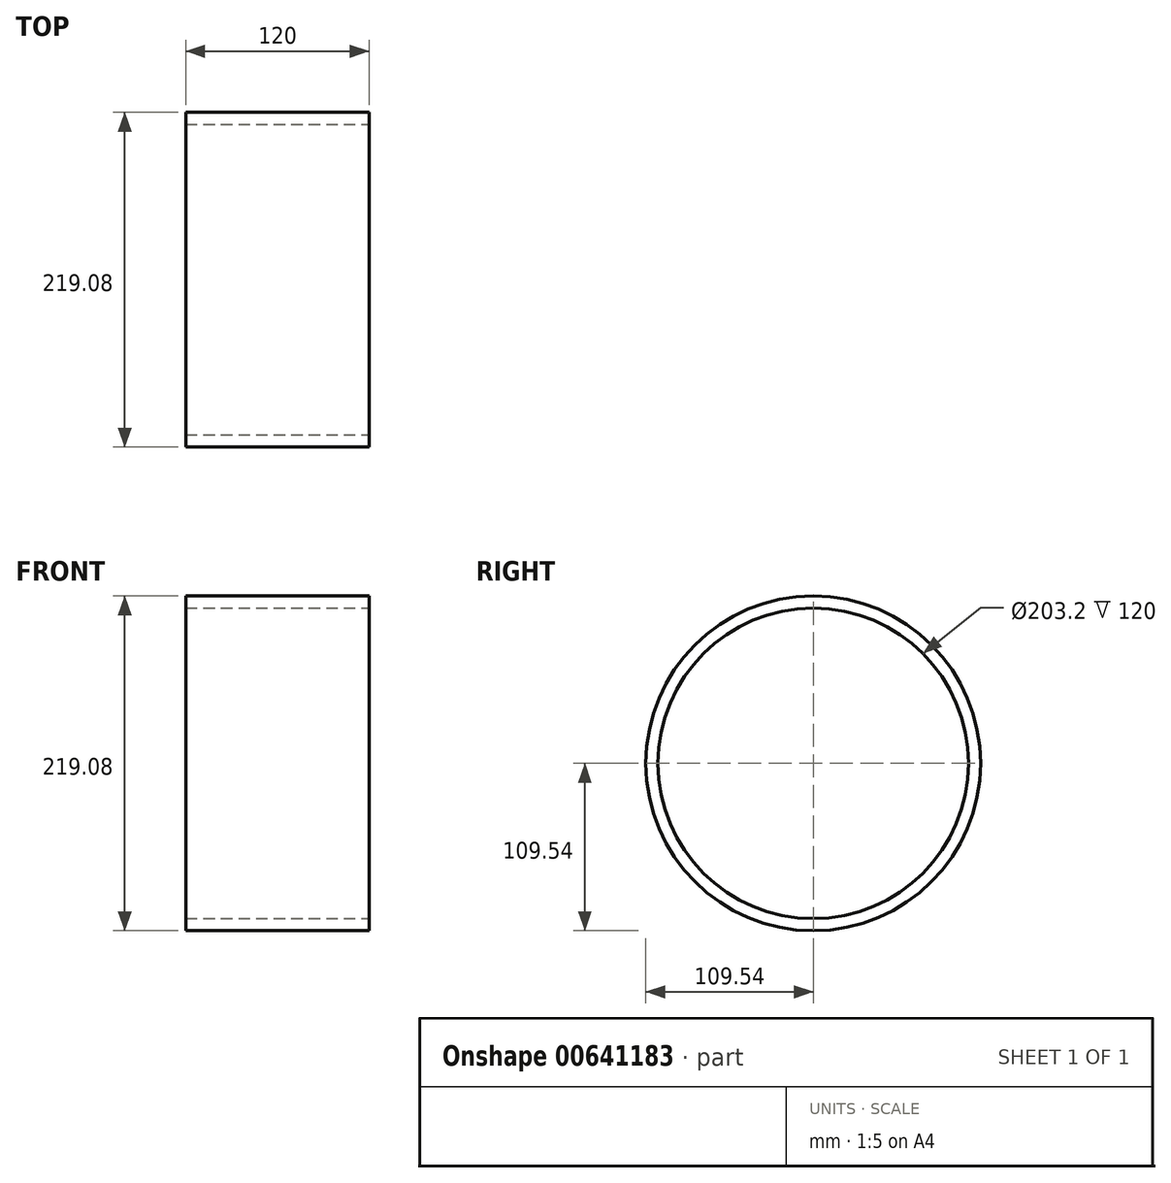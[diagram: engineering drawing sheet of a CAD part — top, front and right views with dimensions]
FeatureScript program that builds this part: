
annotation { "Feature Type Name" : "Feature", "Feature Type Description" : "" }
export const myFeature = defineFeature(function(context is Context, id is Id, definition is map)
    precondition{}
    {
        {
            assignVariable(context, id + "F0", {"name" : "BL", "anyValue" : 120});
        }
        {
            var Q0;
            Q0=qCreatedBy(makeId("Right.planeOp"),FACE);
            var sketch = newSketch(context, id + "F1", { "sketchPlane" : qUnion([Q0])});
            skCircle(sketch, "E0", {"center": v(0, 0) * mm, "radius": 109.54 * mm});
            skCircle(sketch, "E1", {"center": v(0, 0) * mm, "radius": 101.6 * mm});
            skSolve(sketch);
        }
        {
            var Q0;
            Q0=makeQuery(id+"F1.imprint","IMPRINT",FACE,{"disambiguationData":[TD([[makeQuery(id+"F1.imprint","IMPRINT",EDGE,{"derivedFrom":sQuery(id+"F1.wireOp",EDGE,"E0")}),1.0]])]});
            extrude(context, id + "F2", {"entities" : qUnion([Q0]), "oppositeDirection" : true, "depth" : (getVariable(context, 'BL')) * mm, "offsetDistance" : 25.4 * mm});
        }
    });
